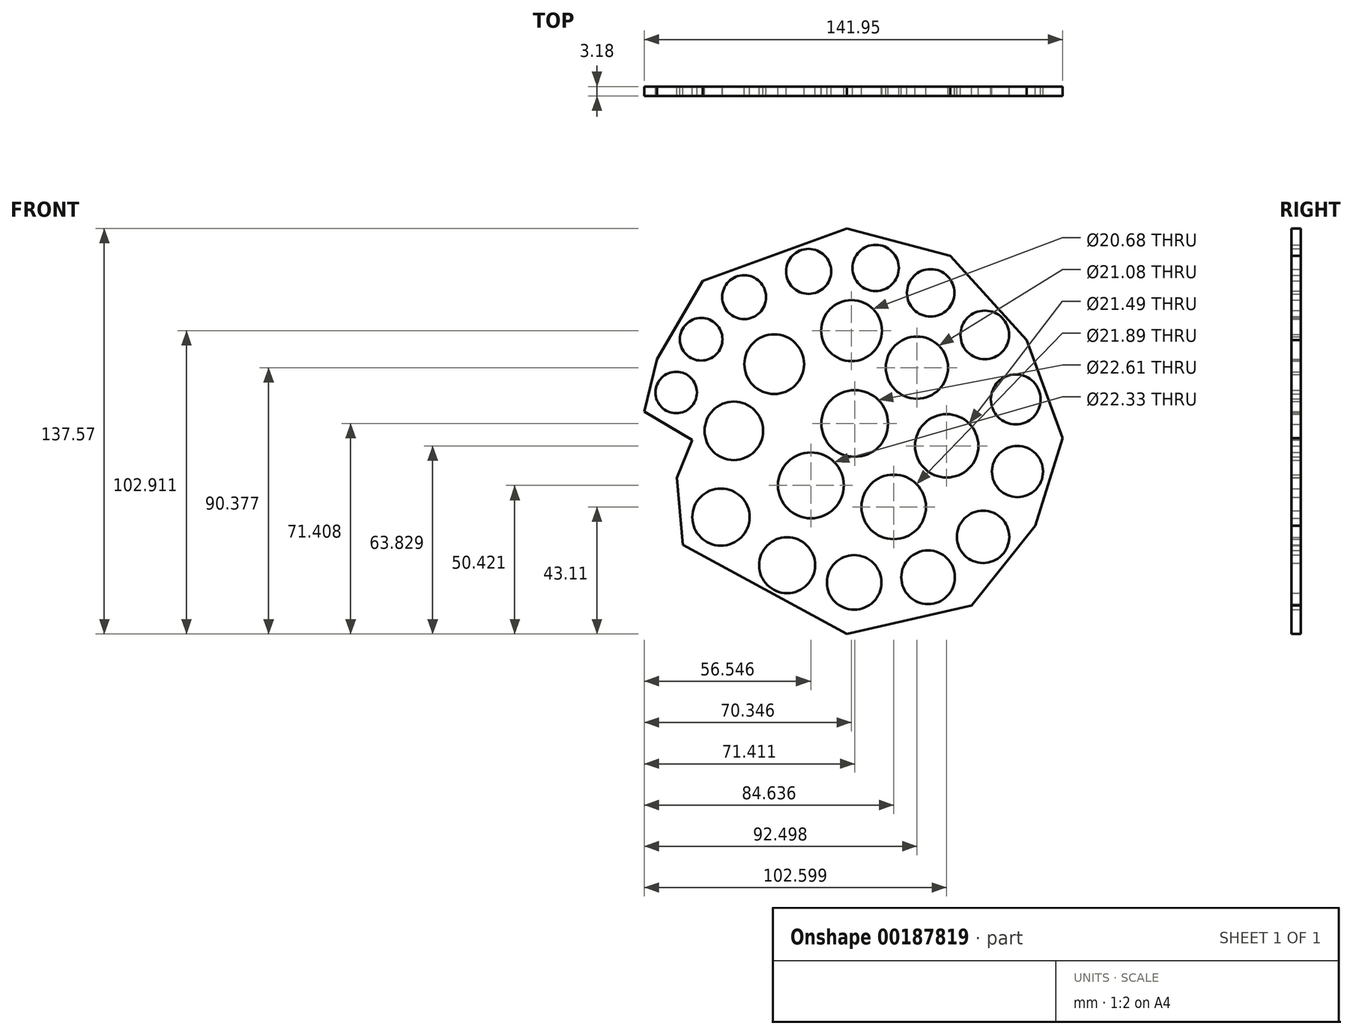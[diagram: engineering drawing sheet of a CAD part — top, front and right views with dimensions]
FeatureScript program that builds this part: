
annotation { "Feature Type Name" : "Feature", "Feature Type Description" : "" }
export const myFeature = defineFeature(function(context is Context, id is Id, definition is map)
    precondition{}
    {
        {
            var Q0;
            Q0=qCreatedBy(makeId("Front.planeOp"),FACE);
            var sketch = newSketch(context, id + "F0", { "sketchPlane" : qUnion([Q0])});
            skCircle(sketch, "E0", {"center": v(-63.44, 13) * mm, "radius": 7.02 * mm});
            skCircle(sketch, "E1", {"center": v(-55, 31.07) * mm, "radius": 7.23 * mm});
            skCircle(sketch, "E2", {"center": v(-40.42, 45.35) * mm, "radius": 7.43 * mm});
            skCircle(sketch, "E3", {"center": v(-18.56, 54.1) * mm, "radius": 7.63 * mm});
            skCircle(sketch, "E4", {"center": v(4.18, 55.26) * mm, "radius": 7.85 * mm});
            skCircle(sketch, "E5", {"center": v(22.83, 46.8) * mm, "radius": 8.05 * mm});
            skCircle(sketch, "E6", {"center": v(41.2, 32.52) * mm, "radius": 8.26 * mm});
            skCircle(sketch, "E7", {"center": v(51.69, 10.66) * mm, "radius": 8.46 * mm});
            skCircle(sketch, "E8", {"center": v(52.27, -13.82) * mm, "radius": 8.67 * mm});
            skCircle(sketch, "E9", {"center": v(40.61, -35.97) * mm, "radius": 8.88 * mm});
            skCircle(sketch, "E10", {"center": v(21.96, -49.67) * mm, "radius": 9.1 * mm});
            skCircle(sketch, "E11", {"center": v(-3.1, -51.42) * mm, "radius": 9.26 * mm});
            skCircle(sketch, "E12", {"center": v(-25.84, -45.6) * mm, "radius": 9.5 * mm});
            skCircle(sketch, "E13", {"center": v(-48.29, -29.27) * mm, "radius": 9.7 * mm});
            skCircle(sketch, "E14", {"center": v(-43.92, 0) * mm, "radius": 9.92 * mm});
            skCircle(sketch, "E15", {"center": v(-30.22, 22.61) * mm, "radius": 10.12 * mm});
            skCircle(sketch, "E16", {"center": v(-3.98, 33.98) * mm, "radius": 10.34 * mm});
            skCircle(sketch, "E17", {"center": v(18.17, 21.45) * mm, "radius": 10.54 * mm});
            skCircle(sketch, "E18", {"center": v(28.27, -5.1) * mm, "radius": 10.74 * mm});
            skCircle(sketch, "E19", {"center": v(10.3, -25.82) * mm, "radius": 10.95 * mm});
            skCircle(sketch, "E20", {"center": v(-2.92, 2.48) * mm, "radius": 11.3 * mm});
            skCircle(sketch, "E21", {"center": v(-17.78, -18.5) * mm, "radius": 11.16 * mm});
            skLineSegment(sketch, "E22", {"start": v(3.2, -11.8) * mm, "end": v(14.28, 5.98) * mm});
            skLineSegment(sketch, "E23", {"start": v(14.28, 5.98) * mm, "end": v(-2.62, 19.67) * mm});
            skLineSegment(sketch, "E24", {"start": v(-2.62, 19.67) * mm, "end": v(-24.2, 3.06) * mm});
            skLineSegment(sketch, "E25", {"start": v(-24.2, 3.06) * mm, "end": v(-32.06, -15.6) * mm});
            skLineSegment(sketch, "E26", {"start": v(-32.06, -15.6) * mm, "end": v(-32.06, -29.58) * mm});
            skLineSegment(sketch, "E27", {"start": v(-32.06, -29.58) * mm, "end": v(0, -39.5) * mm});
            skLineSegment(sketch, "E28", {"start": v(0, -39.5) * mm, "end": v(20.7, -37.16) * mm});
            skLineSegment(sketch, "E29", {"start": v(20.7, -37.16) * mm, "end": v(35.27, -19.97) * mm});
            skLineSegment(sketch, "E30", {"start": v(35.27, -19.97) * mm, "end": v(44.6, -3.06) * mm});
            skLineSegment(sketch, "E31", {"start": v(44.6, -3.06) * mm, "end": v(38.77, 12.1) * mm});
            skLineSegment(sketch, "E32", {"start": v(38.77, 12.1) * mm, "end": v(30.02, 29.58) * mm});
            skLineSegment(sketch, "E33", {"start": v(30.02, 29.58) * mm, "end": v(16.97, 35.4) * mm});
            skLineSegment(sketch, "E34", {"start": v(16.97, 35.4) * mm, "end": v(-5.59, 46.68) * mm});
            skLineSegment(sketch, "E35", {"start": v(-5.59, 46.68) * mm, "end": v(-19, 42.66) * mm});
            skLineSegment(sketch, "E36", {"start": v(-19, 42.66) * mm, "end": v(-40.22, 32.8) * mm});
            skLineSegment(sketch, "E37", {"start": v(-40.22, 32.8) * mm, "end": v(-51, 13.85) * mm});
            skLineSegment(sketch, "E38", {"start": v(-51, 13.85) * mm, "end": v(-63.25, -15.89) * mm});
            skLineSegment(sketch, "E39", {"start": v(-63.25, -15.89) * mm, "end": v(-61.2, -38.62) * mm});
            skLineSegment(sketch, "E40", {"start": v(-61.2, -38.62) * mm, "end": v(-5.59, -68.93) * mm});
            skLineSegment(sketch, "E41", {"start": v(-5.59, -68.93) * mm, "end": v(36.73, -59.32) * mm});
            skLineSegment(sketch, "E42", {"start": v(36.73, -59.32) * mm, "end": v(58.3, -32.2) * mm});
            skLineSegment(sketch, "E43", {"start": v(58.3, -32.2) * mm, "end": v(67.62, -2.48) * mm});
            skLineSegment(sketch, "E44", {"start": v(67.62, -2.48) * mm, "end": v(55.38, 30.75) * mm});
            skLineSegment(sketch, "E45", {"start": v(55.38, 30.75) * mm, "end": v(29.44, 59.32) * mm});
            skLineSegment(sketch, "E46", {"start": v(29.44, 59.32) * mm, "end": v(-5.59, 68.64) * mm});
            skLineSegment(sketch, "E47", {"start": v(-5.59, 68.64) * mm, "end": v(-54.5, 50.86) * mm});
            skLineSegment(sketch, "E48", {"start": v(-54.5, 50.86) * mm, "end": v(-69.95, 24.34) * mm});
            skLineSegment(sketch, "E49", {"start": v(-69.95, 24.34) * mm, "end": v(-74.33, 6.56) * mm});
            skLineSegment(sketch, "E50", {"start": v(-74.33, 6.56) * mm, "end": v(-58, -3.15) * mm});
            skSolve(sketch);
        }
        {
            var Q0;
            Q0 = qSketchRegion(id + "F0", true);
            extrude(context, id + "F1", {"entities" : qUnion([Q0]), "depth" : 3.17 * mm});
        }
    });
